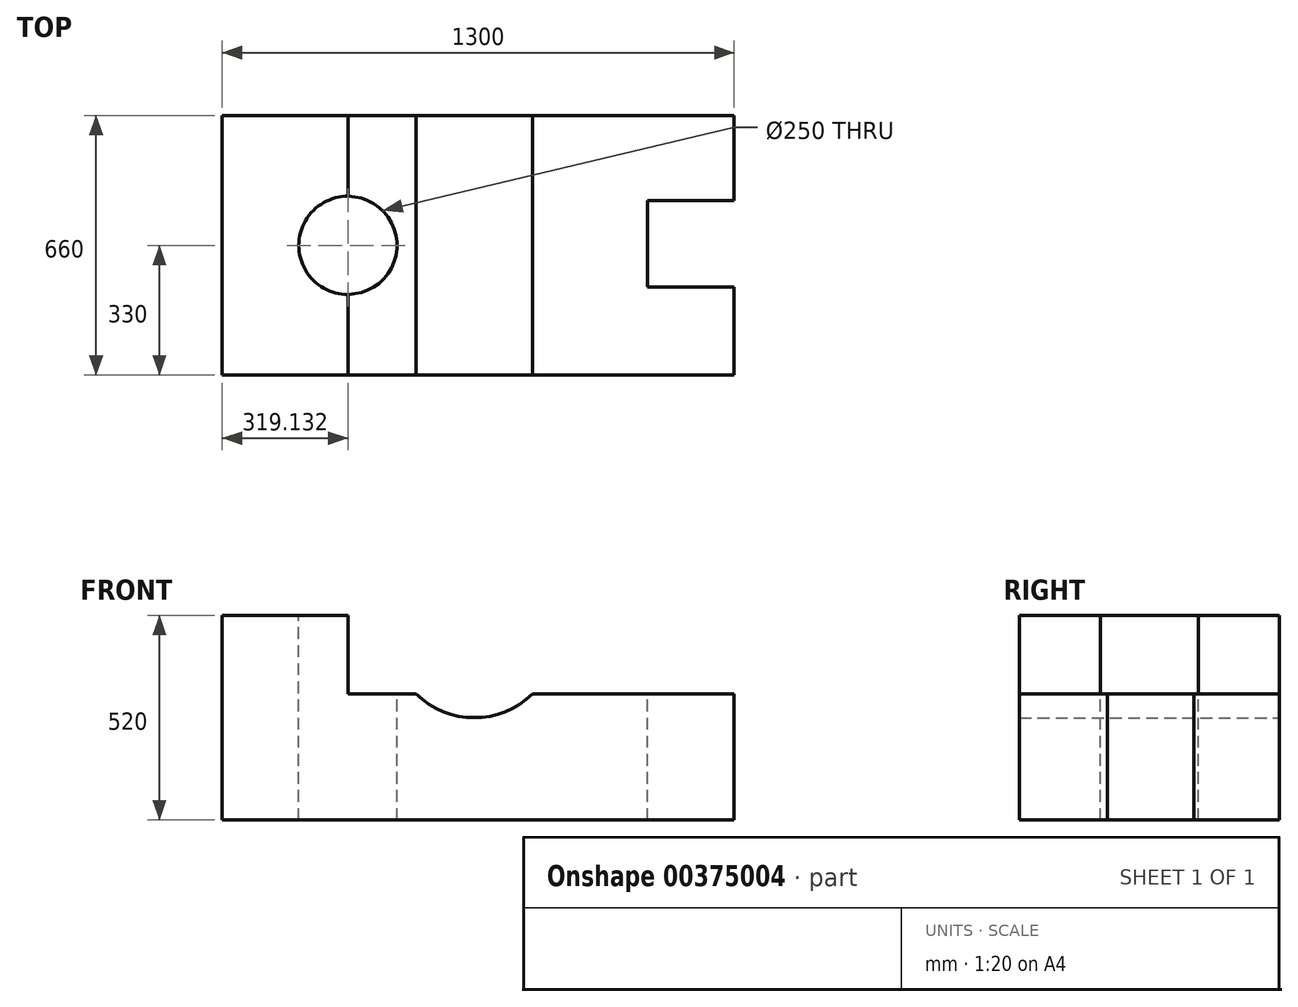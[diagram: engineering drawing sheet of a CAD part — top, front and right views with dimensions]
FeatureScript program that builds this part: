
annotation { "Feature Type Name" : "Feature", "Feature Type Description" : "" }
export const myFeature = defineFeature(function(context is Context, id is Id, definition is map)
    precondition{}
    {
        {
            var Q0;
            Q0=qCreatedBy(makeId("Front.planeOp"),FACE);
            var sketch = newSketch(context, id + "F0", { "sketchPlane" : qUnion([Q0])});
            skLineSegment(sketch, "E0.top", {"start": v(650, -160) * mm, "end": v(-650, -160) * mm});
            skLineSegment(sketch, "E0.left", {"start": v(650, 160) * mm, "end": v(650, -160) * mm});
            skPoint(sketch, "E0.middle", {"position": v(0, 0) * mm});
            skLineSegment(sketch, "E1.top", {"start": v(-650, 360) * mm, "end": v(-330, 360) * mm});
            skLineSegment(sketch, "E1.right", {"start": v(-330, 160) * mm, "end": v(-330, 360) * mm});
            skLineSegment(sketch, "E2", {"start": v(-650, 360) * mm, "end": v(-650, -160) * mm});
            skPoint(sketch, "E3.third.point", {"position": v(71.3, 57.8) * mm});
            skArc(sketch, "E4", {"start": v(-157.36, 160.38) * mm, "mid": v(-10, 100) * mm, "end": v(137.36, 160.38) * mm});
            skLineSegment(sketch, "E5", {"start": v(-330, 160) * mm, "end": v(-157.36, 160.38) * mm});
            skLineSegment(sketch, "E6", {"start": v(137.36, 160.38) * mm, "end": v(650, 160) * mm});
            skSolve(sketch);
        }
        {
            var Q0;
            Q0 = qSketchRegion(id + "F0", true);
            extrude(context, id + "F1", {"entities" : qUnion([Q0]), "endBound" : BoundingType.SYMMETRIC, "depth" : 660 * mm});
        }
        {
            var Q0;
            Q0=qCreatedBy(makeId("Top.planeOp"),FACE);
            var sketch = newSketch(context, id + "F2", { "sketchPlane" : qUnion([Q0])});
            skCircle(sketch, "E7", {"center": v(-330.87, 0) * mm, "radius": 125 * mm});
            skLineSegment(sketch, "E8.bottom", {"start": v(650.39, 113.57) * mm, "end": v(430.39, 113.57) * mm});
            skLineSegment(sketch, "E8.top", {"start": v(650.39, -106.43) * mm, "end": v(430.39, -106.43) * mm});
            skLineSegment(sketch, "E8.left", {"start": v(650.39, 113.57) * mm, "end": v(650.39, -106.43) * mm});
            skLineSegment(sketch, "E8.right", {"start": v(430.39, 113.57) * mm, "end": v(430.39, -106.43) * mm});
            skSolve(sketch);
        }
        {
            var Q0;
            Q0 = qSketchRegion(id + "F2", true);
            extrude(context, id + "F3", {"entities" : qUnion([Q0]), "operationType" : NewBodyOperationType.REMOVE, "endBound" : BoundingType.SYMMETRIC, "oppositeDirection" : true, "depth" : 1000 * mm});
        }
    });
